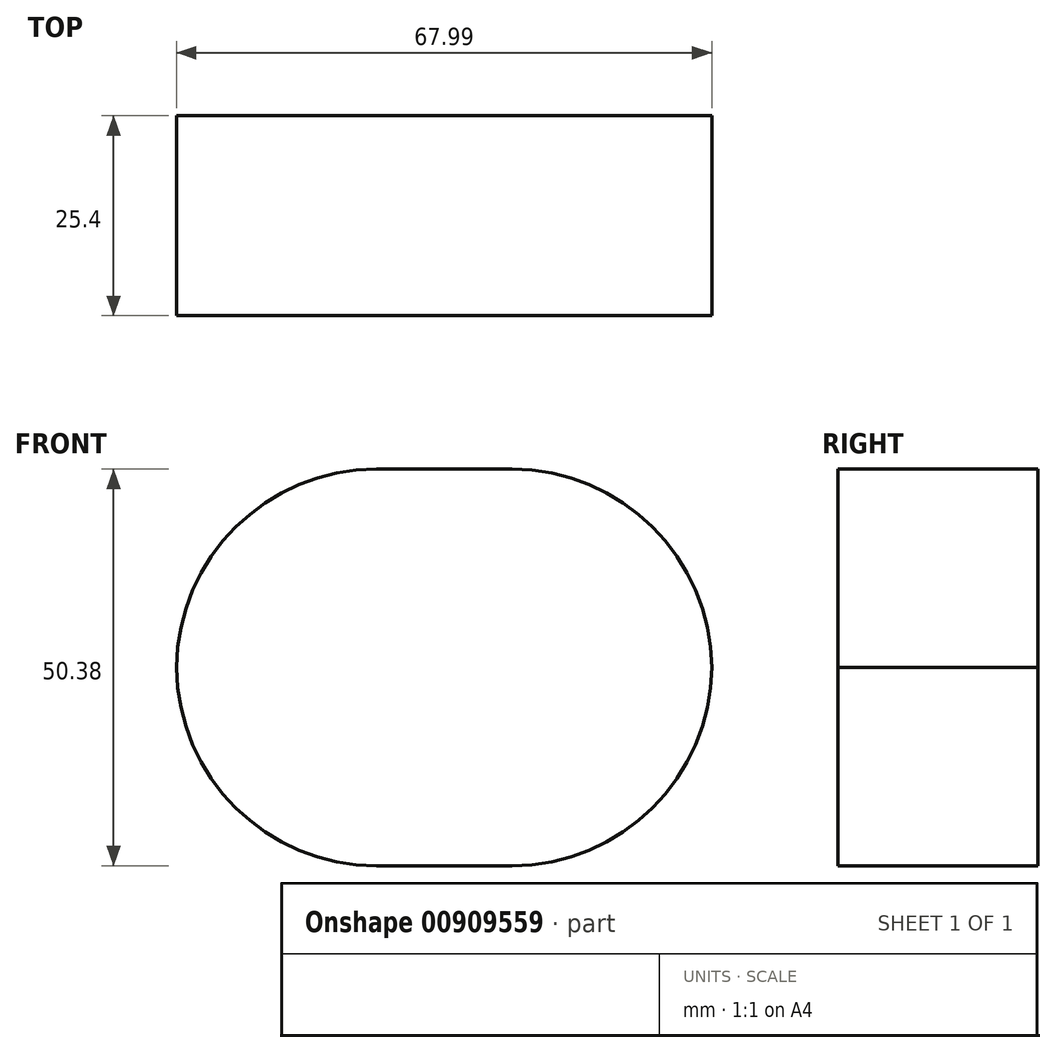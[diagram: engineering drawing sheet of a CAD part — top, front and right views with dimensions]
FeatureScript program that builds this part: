
annotation { "Feature Type Name" : "Feature", "Feature Type Description" : "" }
export const myFeature = defineFeature(function(context is Context, id is Id, definition is map)
    precondition{}
    {
        {
            var Q0;
            Q0=qCreatedBy(makeId("Front.planeOp"),FACE);
            var sketch = newSketch(context, id + "F0", { "sketchPlane" : qUnion([Q0])});
            skLineSegment(sketch, "E0.bottom", {"start": v(0, 0) * mm, "end": v(67.99, 0) * mm});
            skLineSegment(sketch, "E0.top", {"start": v(0, 50.38) * mm, "end": v(67.99, 50.38) * mm});
            skLineSegment(sketch, "E0.left", {"start": v(0, 0) * mm, "end": v(0, 50.38) * mm});
            skLineSegment(sketch, "E0.right", {"start": v(67.99, 0) * mm, "end": v(67.99, 50.38) * mm});
            skSolve(sketch);
        }
        {
            var Q0;
            Q0 = qSketchRegion(id + "F0", true);
            extrude(context, id + "F1", {"entities" : qUnion([Q0]), "depth" : 25.4 * mm, "offsetDistance" : 25.4 * mm});
        }
        {
            var Q0;
            Q0=makeQuery(id+"F1.opExtrude","SWEPT_EDGE",EDGE,{"disambiguationData":[OSD([sQuery(id+"F0.wireOp",EDGE,"E0.top"),sQuery(id+"F0.wireOp",EDGE,"E0.left")])]});
            var Q1;
            Q1=makeQuery(id+"F1.opExtrude","SWEPT_EDGE",EDGE,{"disambiguationData":[OSD([sQuery(id+"F0.wireOp",EDGE,"E0.top"),sQuery(id+"F0.wireOp",EDGE,"E0.right")])]});
            var Q2;
            Q2=makeQuery(id+"F1.opExtrude","SWEPT_EDGE",EDGE,{"disambiguationData":[OSD([sQuery(id+"F0.wireOp",EDGE,"E0.bottom"),sQuery(id+"F0.wireOp",EDGE,"E0.left")])]});
            var Q3;
            Q3=makeQuery(id+"F1.opExtrude","SWEPT_EDGE",EDGE,{"disambiguationData":[OSD([sQuery(id+"F0.wireOp",EDGE,"E0.bottom"),sQuery(id+"F0.wireOp",EDGE,"E0.right")])]});
            fillet(context, id + "F2", {"entities" : qUnion([Q0, Q1, Q2, Q3]), "radius" : 25.4 * mm, "tangentPropagation" : true, "allowEdgeOverflow" : false});
        }
    });
